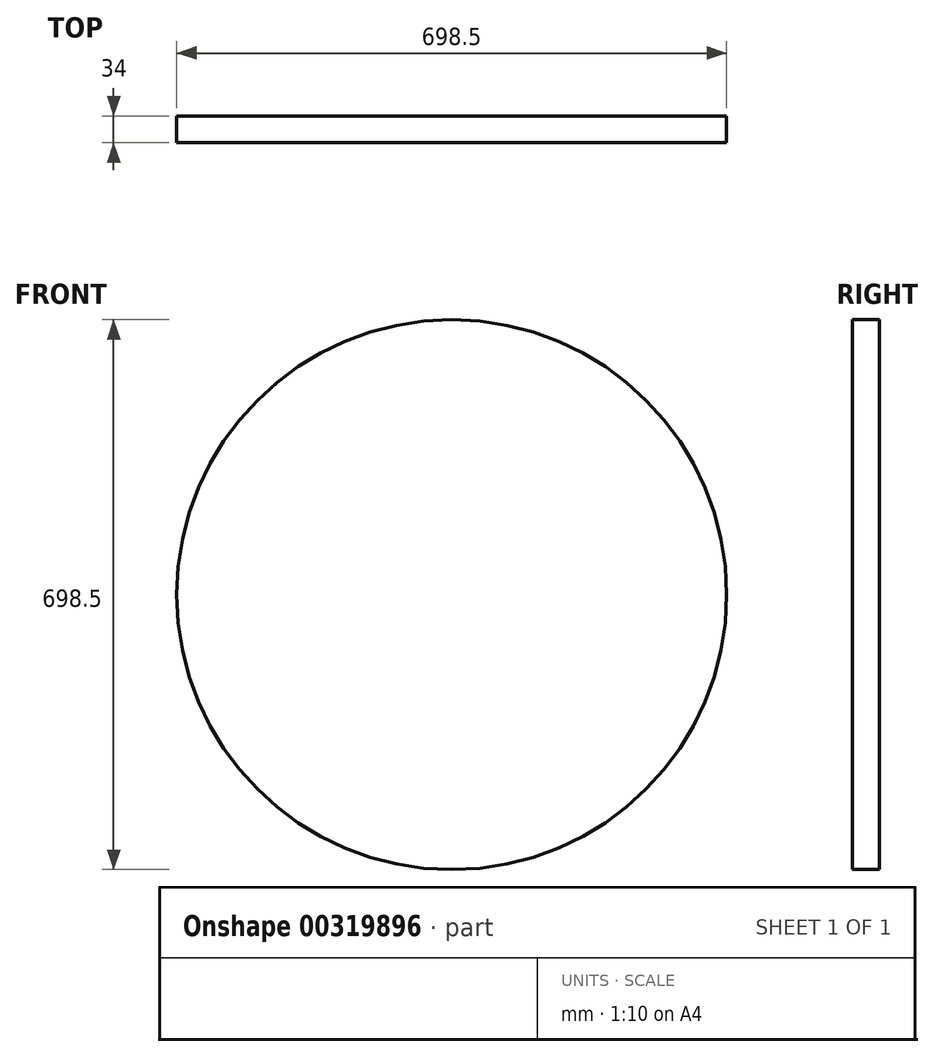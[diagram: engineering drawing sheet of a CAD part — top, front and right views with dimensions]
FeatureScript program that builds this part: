
annotation { "Feature Type Name" : "Feature", "Feature Type Description" : "" }
export const myFeature = defineFeature(function(context is Context, id is Id, definition is map)
    precondition{}
    {
        {
            var Q0;
            Q0=qCreatedBy(makeId("Front.planeOp"),FACE);
            var sketch = newSketch(context, id + "F0", { "sketchPlane" : qUnion([Q0])});
            skCircle(sketch, "E0", {"center": v(0, 0) * mm, "radius": 349.25 * mm});
            skSolve(sketch);
        }
        {
            var Q0;
            Q0=makeQuery(id+"F0.imprint","IMPRINT",FACE,{"disambiguationData":[TD([[makeQuery(id+"F0.imprint","IMPRINT",EDGE,{"derivedFrom":sQuery(id+"F0.wireOp",EDGE,"E0")}),1.0]])]});
            extrude(context, id + "F1", {"entities" : qUnion([Q0]), "depth" : 34 * mm});
        }
    });
